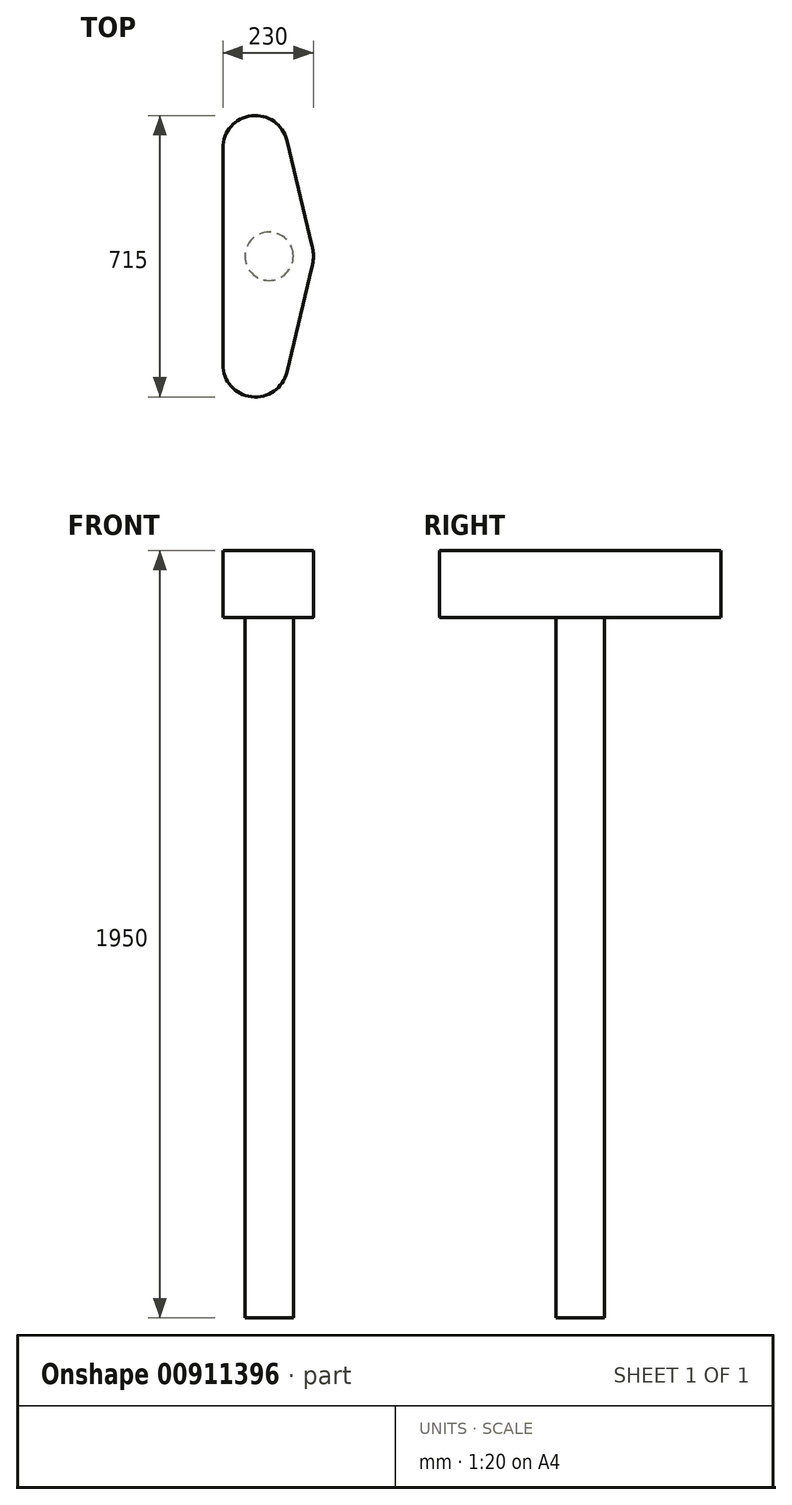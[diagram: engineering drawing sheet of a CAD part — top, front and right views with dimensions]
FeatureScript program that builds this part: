
annotation { "Feature Type Name" : "Feature", "Feature Type Description" : "" }
export const myFeature = defineFeature(function(context is Context, id is Id, definition is map)
    precondition{}
    {
        {
            var Q0;
            Q0=qCreatedBy(makeId("Top.planeOp"),FACE);
            var sketch = newSketch(context, id + "F0", { "sketchPlane" : qUnion([Q0])});
            skArc(sketch, "E0", {"start": v(109.4, -26.2) * mm, "mid": v(112.5, 0) * mm, "end": v(109.4, 26.2) * mm});
            skLineSegment(sketch, "E1", {"start": v(0, 0) * mm, "end": v(112.5, 0) * mm, "construction": true});
            skLineSegment(sketch, "E2", {"start": v(-117.5, 275) * mm, "end": v(-117.5, -171.75) * mm});
            skArc(sketch, "E3", {"start": v(45.23, 294.21) * mm, "mid": v(-44.67, 356.93) * mm, "end": v(-117.5, 275) * mm});
            skLineSegment(sketch, "E4", {"start": v(43.6, 301.01) * mm, "end": v(109.4, 26.2) * mm});
            skArc(sketch, "E5.MirrorC", {"start": v(45.23, -294.21) * mm, "mid": v(-44.67, -356.93) * mm, "end": v(-117.5, -275) * mm});
            skLineSegment(sketch, "E6.MirrorCS", {"start": v(43.6, -301.01) * mm, "end": v(109.4, -26.2) * mm});
            skArc(sketch, "E7.MirrorC", {"start": v(109.4, 26.2) * mm, "mid": v(112.5, 0) * mm, "end": v(109.4, -26.2) * mm});
            skLineSegment(sketch, "E8.MirrorCS", {"start": v(-117.5, -275) * mm, "end": v(-117.5, 171.75) * mm});
            skSolve(sketch);
        }
        {
            var Q0;
            Q0 = qSketchRegion(id + "F0", true);
            extrude(context, id + "F1", {"entities" : qUnion([Q0]), "depth" : 170 * mm, "offsetDistance" : 25 * mm});
        }
        {
            var Q0;
            Q0=makeQuery(id+"F1.opExtrude","CAP_FACE",FACE,{"disambiguationData":[OSD([sQuery(id+"F0.wireOp",EDGE,"E2"),sQuery(id+"F0.wireOp",EDGE,"E3"),sQuery(id+"F0.wireOp",EDGE,"E4"),sQuery(id+"F0.wireOp",EDGE,"E5.MirrorC"),sQuery(id+"F0.wireOp",EDGE,"E6.MirrorCS"),sQuery(id+"F0.wireOp",EDGE,"E7.MirrorC"),sQuery(id+"F0.wireOp",EDGE,"E8.MirrorCS")])],"isStart":true});
            var sketch = newSketch(context, id + "F2", { "sketchPlane" : qUnion([Q0])});
            skCircle(sketch, "E9", {"center": v(0, 0) * mm, "radius": 61.5 * mm});
            skSolve(sketch);
        }
        {
            var Q0;
            Q0 = qSketchRegion(id + "F2", true);
            extrude(context, id + "F3", {"entities" : qUnion([Q0]), "depth" : 1780 * mm, "offsetDistance" : 25 * mm});
        }
    });
